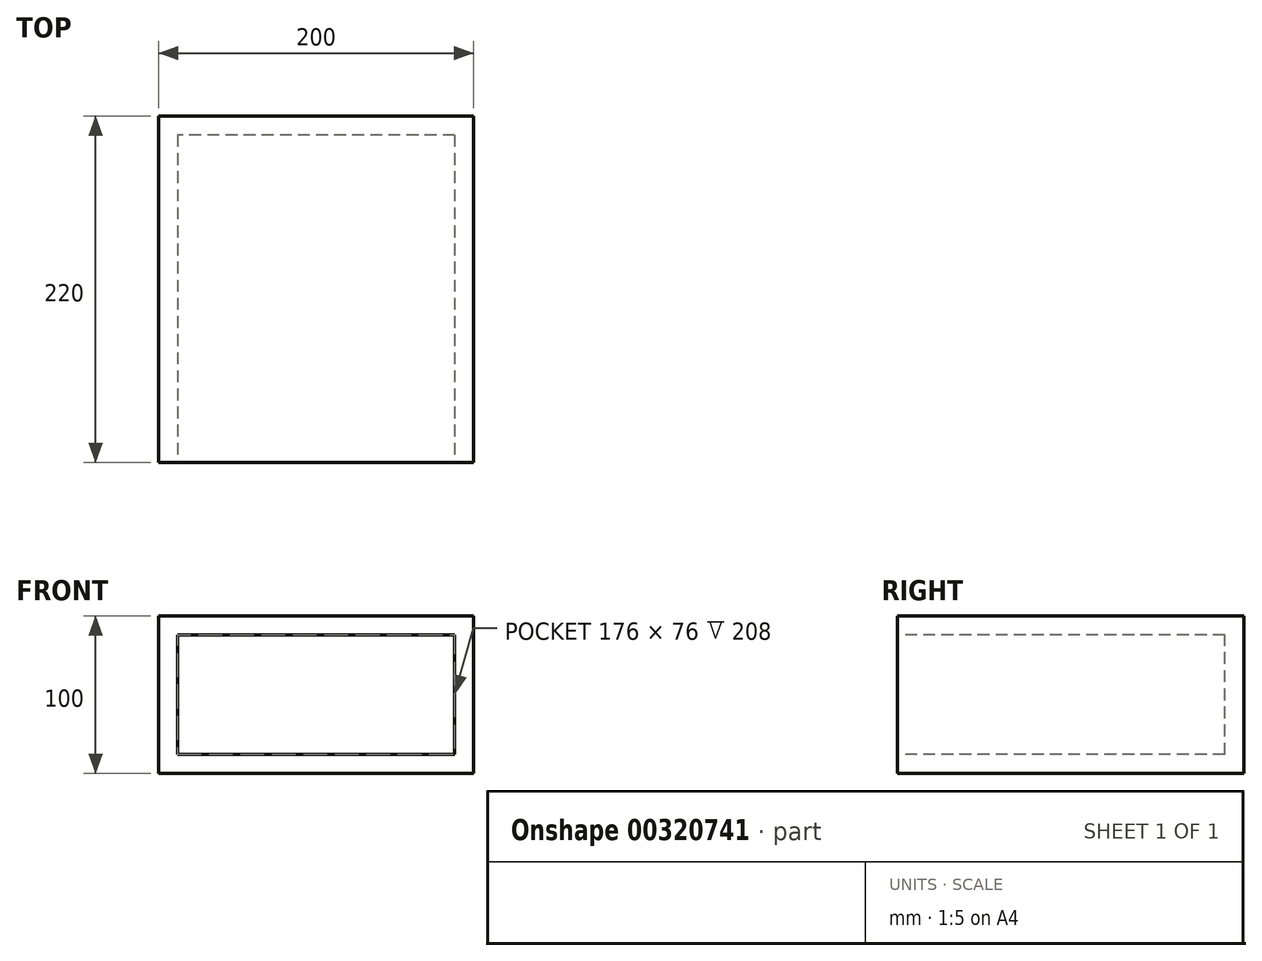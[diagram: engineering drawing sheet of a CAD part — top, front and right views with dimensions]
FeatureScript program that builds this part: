
annotation { "Feature Type Name" : "Feature", "Feature Type Description" : "" }
export const myFeature = defineFeature(function(context is Context, id is Id, definition is map)
    precondition{}
    {
        {
            var Q0;
            Q0=qCreatedBy(makeId("Front.planeOp"),FACE);
            var sketch = newSketch(context, id + "F0", { "sketchPlane" : qUnion([Q0])});
            skLineSegment(sketch, "E0.bottom", {"start": v(100, -50) * mm, "end": v(-100, -50) * mm});
            skLineSegment(sketch, "E0.top", {"start": v(100, 50) * mm, "end": v(-100, 50) * mm});
            skLineSegment(sketch, "E0.left", {"start": v(100, -50) * mm, "end": v(100, 50) * mm});
            skLineSegment(sketch, "E0.right", {"start": v(-100, -50) * mm, "end": v(-100, 50) * mm});
            skPoint(sketch, "E0.middle", {"position": v(0, 0) * mm});
            skSolve(sketch);
        }
        {
            var Q0;
            Q0=makeQuery(id+"F0.imprint","IMPRINT",FACE,{"disambiguationData":[TD([[makeQuery(id+"F0.imprint","IMPRINT",EDGE,{"derivedFrom":sQuery(id+"F0.wireOp",EDGE,"E0.bottom")}),-1.0]])]});
            extrude(context, id + "F1", {"entities" : qUnion([Q0]), "oppositeDirection" : true, "depth" : 220 * mm});
        }
        {
            var Q0;
            Q0=makeQuery(id+"F1.opExtrude","CAP_FACE",FACE,{"disambiguationData":[OSD([sQuery(id+"F0.wireOp",EDGE,"E0.bottom"),sQuery(id+"F0.wireOp",EDGE,"E0.top"),sQuery(id+"F0.wireOp",EDGE,"E0.left"),sQuery(id+"F0.wireOp",EDGE,"E0.right")])],"isStart":true});
            shell(context, id + "F2", {"entities" : qUnion([Q0]), "thickness" : 12 * mm});
        }
    });
